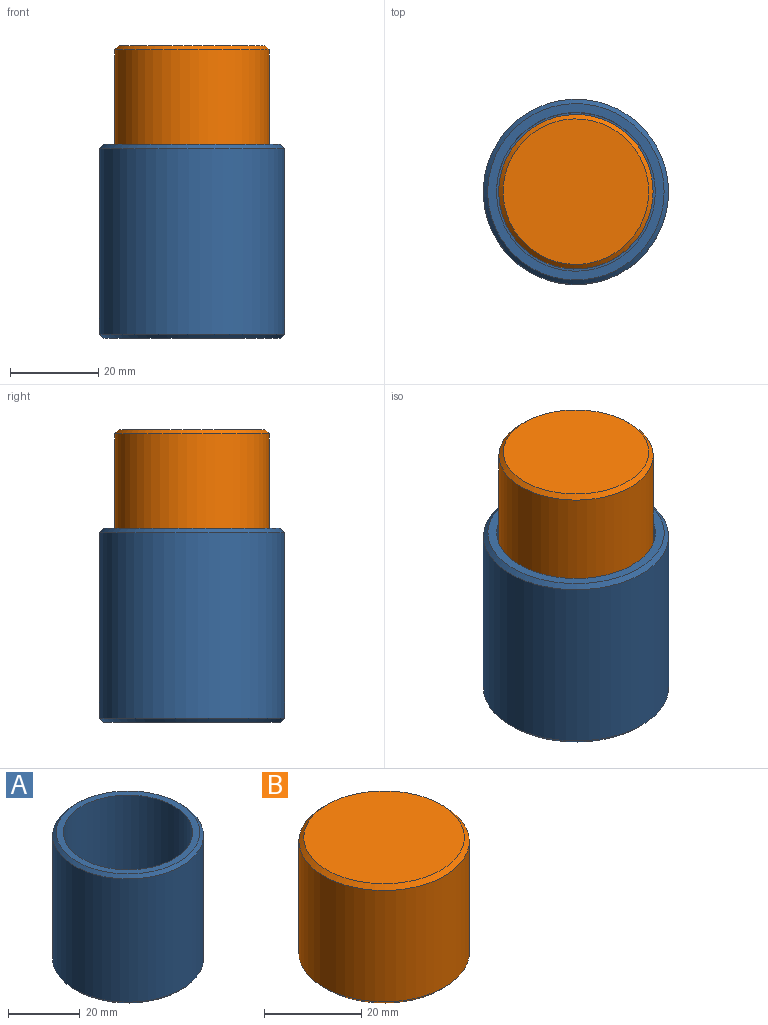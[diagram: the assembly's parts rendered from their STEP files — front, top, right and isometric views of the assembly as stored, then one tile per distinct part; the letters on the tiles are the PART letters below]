
ASSEMBLY  parts=2 mates=1
PART A: 8 faces, bbox 42x42x44 mm
  f0: plane 36x36mm, normal (0,0,1), area 931.3mm2, adj f1,f4
  f1: cylinder r=5.25mm len=10.5mm, axis (0,0,1), area 131.9mm2, adj f0,f3
  f2: cylinder r=21mm len=42mm, axis (0,0,1), area 5541.8mm2, adj f6,f7
  f3: plane 40x40mm, normal (0,0,-1), area 1170mm2, adj f1,f6
  f4: cylinder r=18mm len=40mm, axis (0,0,-1), area 4523.9mm2, adj f0,f5
  f5: plane 40x40mm, normal (0,0,1), area 238.8mm2, adj f4,f7
  f6: cone r=21mm half-angle=45deg, axis (0,0,1), area 182.2mm2, adj f2,f3
  f7: cone r=20mm half-angle=45deg, axis (0,0,-1), area 182.2mm2, adj f2,f5
PART B: 5 faces, bbox 35x35x30 mm
  f0: cylinder r=17.5mm len=35mm, axis (0,0,-1), area 3078.8mm2, adj f3,f4
  f1: plane 33x33mm, normal (0,0,1), area 855.3mm2, adj f4
  f2: plane 33x33mm, normal (0,0,-1), area 855.3mm2, adj f3
  f3: cone r=17.5mm half-angle=45deg, axis (0,0,1), area 151.1mm2, adj f0,f2
  f4: cone r=16.5mm half-angle=45deg, axis (0,0,-1), area 151.1mm2, adj f0,f1
PLACE A t=(-5.42,-3.92,-9.34)mm
PLACE B t=(-5.42,-3.92,23.06)mm
MATE slider A.f4 <-> B.f0  axis (0,0,-1) through (-5.42,-3.92,30.66)mm
